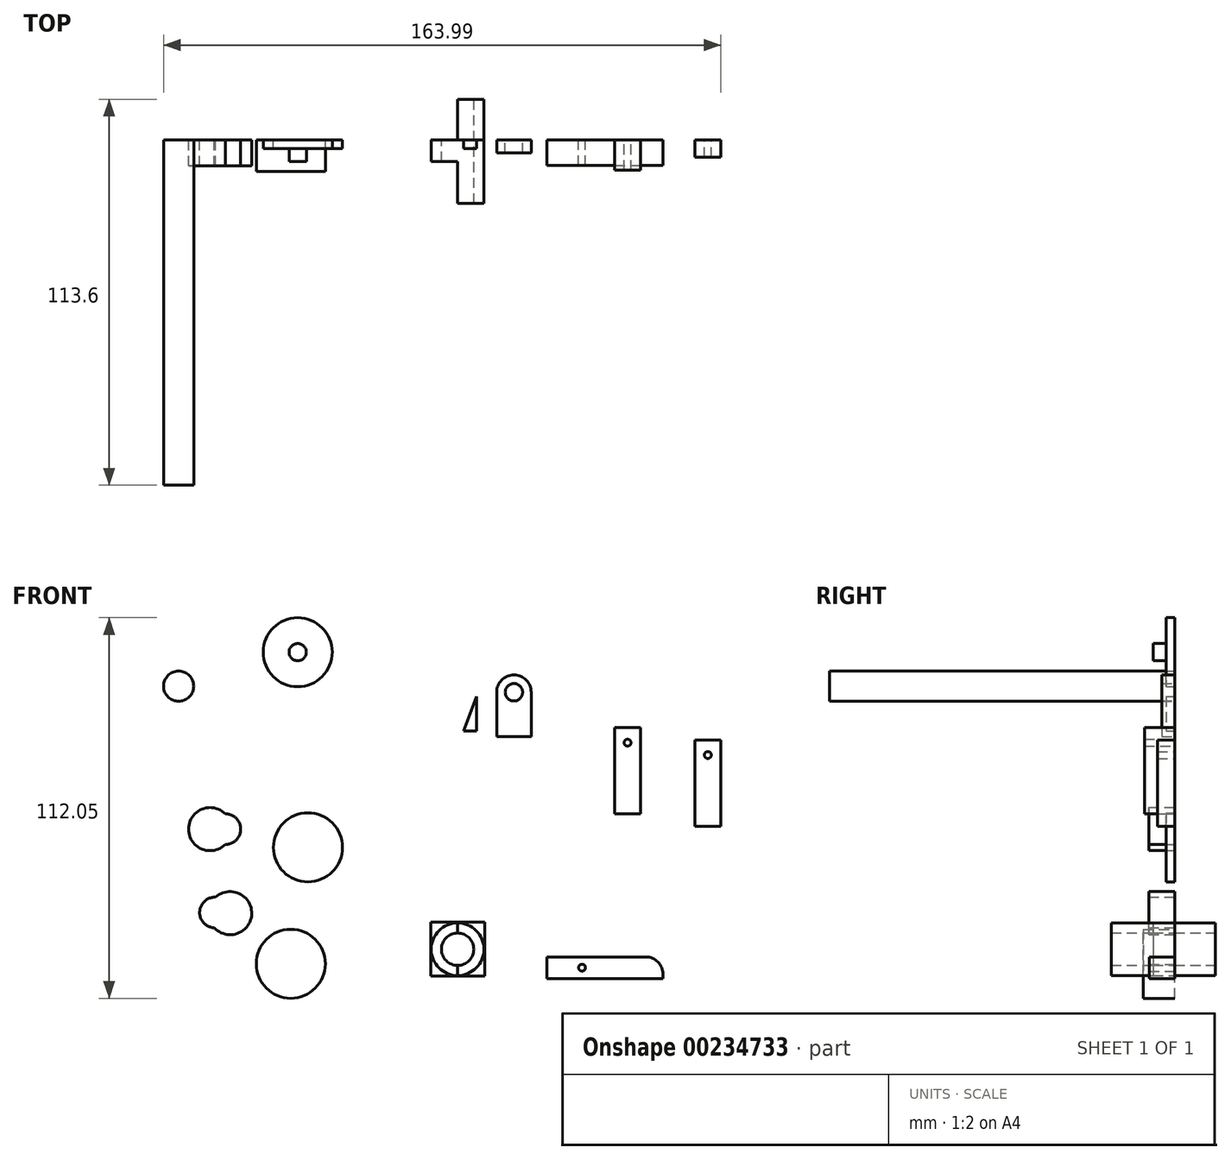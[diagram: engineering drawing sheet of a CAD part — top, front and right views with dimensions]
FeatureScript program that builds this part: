
annotation { "Feature Type Name" : "Feature", "Feature Type Description" : "" }
export const myFeature = defineFeature(function(context is Context, id is Id, definition is map)
    precondition{}
    {
        {
            var Q0;
            Q0=qCreatedBy(makeId("Front.planeOp"),FACE);
            var sketch = newSketch(context, id + "F0", { "sketchPlane" : qUnion([Q0])});
            skLineSegment(sketch, "E0.bottom", {"start": v(-88.6, 67.1) * mm, "end": v(-25.1, 67.1) * mm});
            skLineSegment(sketch, "E0.top", {"start": v(-88.6, 60.75) * mm, "end": v(-25.1, 60.75) * mm});
            skLineSegment(sketch, "E0.left", {"start": v(-88.6, 67.1) * mm, "end": v(-88.6, 60.75) * mm});
            skLineSegment(sketch, "E0.right", {"start": v(-25.1, 67.1) * mm, "end": v(-25.1, 60.75) * mm});
            skLineSegment(sketch, "E1.bottom", {"start": v(5.5, -31.9) * mm, "end": v(21.38, -31.9) * mm});
            skLineSegment(sketch, "E1.top", {"start": v(5.5, -47.78) * mm, "end": v(21.38, -47.78) * mm});
            skLineSegment(sketch, "E1.left", {"start": v(5.5, -31.9) * mm, "end": v(5.5, -47.78) * mm});
            skLineSegment(sketch, "E1.right", {"start": v(21.38, -31.9) * mm, "end": v(21.38, -47.78) * mm});
            skLineSegment(sketch, "E2.bottom", {"start": v(39.75, -42.1) * mm, "end": v(73.87, -42.1) * mm});
            skLineSegment(sketch, "E2.top", {"start": v(39.75, -48.45) * mm, "end": v(73.87, -48.45) * mm});
            skLineSegment(sketch, "E2.left", {"start": v(39.75, -42.1) * mm, "end": v(39.75, -48.45) * mm});
            skLineSegment(sketch, "E2.right", {"start": v(73.87, -42.1) * mm, "end": v(73.87, -48.45) * mm});
            skCircle(sketch, "E3", {"center": v(13.44, -39.84) * mm, "radius": 4.76 * mm});
            skPoint(sketch, "E3.centerSnap0", {"position": v(13.44, -31.9) * mm});
            skPoint(sketch, "E3.centerSnap1", {"position": v(5.5, -39.84) * mm});
            skCircle(sketch, "E4", {"center": v(-53.5, -29.22) * mm, "radius": 6.35 * mm});
            skArc(sketch, "E5", {"start": v(-57.8, -24.54) * mm, "mid": v(-62.48, -28.85) * mm, "end": v(-58.17, -33.52) * mm});
            skCircle(sketch, "E6", {"center": v(-35.65, -44.13) * mm, "radius": 10.16 * mm});
            skCircle(sketch, "E7", {"center": v(50.06, -45.27) * mm, "radius": 1.02 * mm});
            skCircle(sketch, "E8", {"center": v(-30.62, -9.86) * mm, "radius": 10.16 * mm});
            skCircle(sketch, "E9", {"center": v(-33.63, 47.6) * mm, "radius": 10.16 * mm});
            skCircle(sketch, "E10", {"center": v(-33.63, 47.6) * mm, "radius": 2.54 * mm});
            skLineSegment(sketch, "E11.bottom", {"start": v(24.93, 40.87) * mm, "end": v(35.1, 40.87) * mm});
            skLineSegment(sketch, "E11.top", {"start": v(24.93, 22.76) * mm, "end": v(35.1, 22.76) * mm});
            skLineSegment(sketch, "E11.left", {"start": v(24.93, 40.87) * mm, "end": v(24.93, 22.76) * mm});
            skLineSegment(sketch, "E11.right", {"start": v(35.1, 40.87) * mm, "end": v(35.1, 22.76) * mm});
            skCircle(sketch, "E12", {"center": v(30.01, 35.8) * mm, "radius": 2.56 * mm});
            skLineSegment(sketch, "E13", {"start": v(30.01, 35.8) * mm, "end": v(35.1, 35.8) * mm});
            skLineSegment(sketch, "E14", {"start": v(30.01, 35.8) * mm, "end": v(24.93, 35.8) * mm});
            skLineSegment(sketch, "E15", {"start": v(19.02, 34.56) * mm, "end": v(19.02, 24.4) * mm});
            skLineSegment(sketch, "E16", {"start": v(19.02, 24.4) * mm, "end": v(15.21, 24.4) * mm});
            skLineSegment(sketch, "E17", {"start": v(15.21, 24.4) * mm, "end": v(19.02, 34.56) * mm});
            skCircle(sketch, "E18", {"center": v(-59.4, -4.5) * mm, "radius": 6.35 * mm});
            skArc(sketch, "E19", {"start": v(-54.9, -8.98) * mm, "mid": v(-50.41, -4.5) * mm, "end": v(-54.9, 0) * mm});
            skLineSegment(sketch, "E20.bottom", {"start": v(83.25, 21.77) * mm, "end": v(90.87, 21.77) * mm});
            skLineSegment(sketch, "E20.top", {"start": v(83.25, -3.63) * mm, "end": v(90.87, -3.63) * mm});
            skLineSegment(sketch, "E20.left", {"start": v(83.25, 21.77) * mm, "end": v(83.25, -3.63) * mm});
            skLineSegment(sketch, "E20.right", {"start": v(90.87, 21.77) * mm, "end": v(90.87, -3.63) * mm});
            skCircle(sketch, "E21", {"center": v(87.06, 17.33) * mm, "radius": 1.02 * mm});
            skLineSegment(sketch, "E22", {"start": v(86.05, 17.33) * mm, "end": v(83.25, 17.33) * mm});
            skLineSegment(sketch, "E23", {"start": v(88.08, 17.33) * mm, "end": v(90.87, 17.33) * mm});
            skPoint(sketch, "E23.endSnap0", {"position": v(90.87, 9.07) * mm});
            skLineSegment(sketch, "E24.bottom", {"start": v(59.65, 25.4) * mm, "end": v(67.27, 25.4) * mm});
            skLineSegment(sketch, "E24.top", {"start": v(59.65, 0) * mm, "end": v(67.27, 0) * mm});
            skLineSegment(sketch, "E24.left", {"start": v(59.65, 25.4) * mm, "end": v(59.65, 0) * mm});
            skLineSegment(sketch, "E24.right", {"start": v(67.27, 25.4) * mm, "end": v(67.27, 0) * mm});
            skCircle(sketch, "E25", {"center": v(63.44, 20.96) * mm, "radius": 1.02 * mm});
            skLineSegment(sketch, "E26", {"start": v(62.47, 21.24) * mm, "end": v(59.65, 21.24) * mm});
            skLineSegment(sketch, "E27", {"start": v(64.46, 21) * mm, "end": v(67.27, 21) * mm});
            skCircle(sketch, "E28", {"center": v(-68.68, 37.58) * mm, "radius": 4.45 * mm});
            skCircle(sketch, "E29", {"center": v(13.44, -39.84) * mm, "radius": 7.75 * mm});
            skLineSegment(sketch, "E30", {"start": v(13.44, -35.08) * mm, "end": v(13.44, -32.1) * mm});
            skLineSegment(sketch, "E31", {"start": v(13.44, -44.6) * mm, "end": v(13.44, -47.6) * mm});
            skSolve(sketch);
        }
        {
            var Q0;
            Q0=makeQuery(id+"F0.imprint","IMPRINT",FACE,{"disambiguationData":[TD([[makeQuery(id+"F0.imprint","IMPRINT",EDGE,{"derivedFrom":sQuery(id+"F0.wireOp",EDGE,"E1.bottom")}),-1.0]])]});
            extrude(context, id + "F1", {"entities" : qUnion([Q0]), "depth" : 1 / 101.6 * mm});
        }
        {
            var Q0;
            Q0=makeQuery(id+"F0.imprint","IMPRINT",FACE,{"disambiguationData":[TD([[makeQuery(id+"F0.imprint","IMPRINT",EDGE,{"derivedFrom":sQuery(id+"F0.wireOp",EDGE,"E2.bottom")}),-1.0]])]});
            extrude(context, id + "F2", {"entities" : qUnion([Q0]), "depth" : 7.52 * mm});
        }
        {
            var Q0;
            {var subQ0=sQuery(id+"F0.wireOp",EDGE,"E5");var subQ1=sQuery(id+"F0.wireOp",EDGE,"E4");var subQ2=makeQuery(id+"F0.imprint","INTERSECT",VERTEX,{"disambiguationData":[OD(0.0)],"derivedFrom":[subQ1,subQ0]});Q0=makeQuery(id+"F0.imprint","IMPRINT",FACE,{"disambiguationData":[TD([[makeQuery(id+"F0.imprint","IMPRINT",EDGE,{"disambiguationData":[TD([[subQ2,-1.0]])],"derivedFrom":subQ1}),1.0]])]});}
            var Q1;
            {var subQ0=sQuery(id+"F0.wireOp",EDGE,"E5");Q1=makeQuery(id+"F0.imprint","IMPRINT",FACE,{"disambiguationData":[TD([[makeQuery(id+"F0.imprint","IMPRINT",EDGE,{"derivedFrom":subQ0}),1.0]])]});}
            extrude(context, id + "F3", {"entities" : qUnion([Q0, Q1]), "depth" : 7.62 * mm});
        }
        {
            var Q0;
            Q0=makeQuery(id+"F0.imprint","IMPRINT",FACE,{"disambiguationData":[TD([[makeQuery(id+"F0.imprint","IMPRINT",EDGE,{"derivedFrom":sQuery(id+"F0.wireOp",EDGE,"E6")}),1.0]])]});
            extrude(context, id + "F4", {"entities" : qUnion([Q0]), "depth" : 9.27 * mm});
        }
        {
            var Q0;
            Q0=makeQuery(id+"F2.opExtrude","SWEPT_EDGE",EDGE,{"disambiguationData":[OSD([sQuery(id+"F0.wireOp",EDGE,"E2.bottom"),sQuery(id+"F0.wireOp",EDGE,"E2.right")])]});
            fillet(context, id + "F5", {"entities" : qUnion([Q0]), "radius" : 5.08 * mm, "tangentPropagation" : true, "allowEdgeOverflow" : false});
        }
        {
            var Q0;
            Q0=makeQuery(id+"F0.imprint","IMPRINT",FACE,{"disambiguationData":[TD([[makeQuery(id+"F0.imprint","IMPRINT",EDGE,{"derivedFrom":sQuery(id+"F0.wireOp",EDGE,"E8")}),1.0]])]});
            extrude(context, id + "F6", {"entities" : qUnion([Q0]), "depth" : 2.54 * mm});
        }
        {
            var Q0;
            Q0=makeQuery(id+"F0.imprint","IMPRINT",FACE,{"disambiguationData":[TD([[makeQuery(id+"F0.imprint","IMPRINT",EDGE,{"derivedFrom":sQuery(id+"F0.wireOp",EDGE,"E10")}),1.0]])]});
            extrude(context, id + "F7", {"entities" : qUnion([Q0]), "depth" : 6.35 * mm});
        }
        {
            var Q0;
            Q0=makeQuery(id+"F0.imprint","IMPRINT",FACE,{"disambiguationData":[TD([[makeQuery(id+"F0.imprint","IMPRINT",EDGE,{"derivedFrom":sQuery(id+"F0.wireOp",EDGE,"E9")}),1.0]])]});
            extrude(context, id + "F8", {"entities" : qUnion([Q0]), "operationType" : NewBodyOperationType.ADD, "depth" : 2.54 * mm});
        }
        {
            var Q0;
            {var subQ6=sQuery(id+"F0.wireOp",EDGE,"E11.top");Q0=makeQuery(id+"F0.imprint","IMPRINT",FACE,{"disambiguationData":[TD([[makeQuery(id+"F0.imprint","IMPRINT",EDGE,{"derivedFrom":subQ6}),1.0]])]});}
            var Q1;
            {var subQ6=sQuery(id+"F0.wireOp",EDGE,"E11.bottom");Q1=makeQuery(id+"F0.imprint","IMPRINT",FACE,{"disambiguationData":[TD([[makeQuery(id+"F0.imprint","IMPRINT",EDGE,{"derivedFrom":subQ6}),-1.0]])]});}
            extrude(context, id + "F9", {"entities" : qUnion([Q0, Q1]), "depth" : 3.8 * mm});
        }
        {
            var Q0;
            Q0=makeQuery(id+"F0.imprint","IMPRINT",FACE,{"disambiguationData":[TD([[makeQuery(id+"F0.imprint","IMPRINT",EDGE,{"derivedFrom":sQuery(id+"F0.wireOp",EDGE,"E15")}),-1.0]])]});
            extrude(context, id + "F10", {"entities" : qUnion([Q0]), "depth" : 2.54 * mm});
        }
        {
            var Q0;
            Q0=makeQuery(id+"F9.opExtrude","SWEPT_EDGE",EDGE,{"disambiguationData":[OSD([sQuery(id+"F0.wireOp",EDGE,"E11.bottom"),sQuery(id+"F0.wireOp",EDGE,"E11.right")])]});
            var Q1;
            Q1=makeQuery(id+"F9.opExtrude","SWEPT_EDGE",EDGE,{"disambiguationData":[OSD([sQuery(id+"F0.wireOp",EDGE,"E11.bottom"),sQuery(id+"F0.wireOp",EDGE,"E11.left")])]});
            fillet(context, id + "F11", {"entities" : qUnion([Q0, Q1]), "radius" : 5.08 * mm, "tangentPropagation" : true, "allowEdgeOverflow" : false});
        }
        {
            var Q0;
            {var subQ0=sQuery(id+"F0.wireOp",EDGE,"E19");var subQ1=sQuery(id+"F0.wireOp",EDGE,"E18");var subQ2=makeQuery(id+"F0.imprint","INTERSECT",VERTEX,{"disambiguationData":[OD(0.0)],"derivedFrom":[subQ1,subQ0]});Q0=makeQuery(id+"F0.imprint","IMPRINT",FACE,{"disambiguationData":[TD([[makeQuery(id+"F0.imprint","IMPRINT",EDGE,{"disambiguationData":[TD([[subQ2,1.0]])],"derivedFrom":subQ1}),1.0]])]});}
            var Q1;
            {var subQ0=sQuery(id+"F0.wireOp",EDGE,"E19");Q1=makeQuery(id+"F0.imprint","IMPRINT",FACE,{"disambiguationData":[TD([[makeQuery(id+"F0.imprint","IMPRINT",EDGE,{"derivedFrom":subQ0}),1.0]])]});}
            extrude(context, id + "F12", {"entities" : qUnion([Q0, Q1]), "depth" : 7.62 * mm});
        }
        {
            var Q0;
            {var subQ4=sQuery(id+"F0.wireOp",EDGE,"E20.bottom");Q0=makeQuery(id+"F0.imprint","IMPRINT",FACE,{"disambiguationData":[TD([[makeQuery(id+"F0.imprint","IMPRINT",EDGE,{"derivedFrom":subQ4}),-1.0]])]});}
            var Q1;
            {var subQ4=sQuery(id+"F0.wireOp",EDGE,"E20.top");Q1=makeQuery(id+"F0.imprint","IMPRINT",FACE,{"disambiguationData":[TD([[makeQuery(id+"F0.imprint","IMPRINT",EDGE,{"derivedFrom":subQ4}),1.0]])]});}
            extrude(context, id + "F13", {"entities" : qUnion([Q0, Q1]), "depth" : 5.08 * mm});
        }
        {
            var Q0;
            {var subQ4=sQuery(id+"F0.wireOp",EDGE,"E24.bottom");Q0=makeQuery(id+"F0.imprint","IMPRINT",FACE,{"disambiguationData":[TD([[makeQuery(id+"F0.imprint","IMPRINT",EDGE,{"derivedFrom":subQ4}),-1.0]])]});}
            var Q1;
            {var subQ4=sQuery(id+"F0.wireOp",EDGE,"E24.top");Q1=makeQuery(id+"F0.imprint","IMPRINT",FACE,{"disambiguationData":[TD([[makeQuery(id+"F0.imprint","IMPRINT",EDGE,{"derivedFrom":subQ4}),1.0]])]});}
            extrude(context, id + "F14", {"entities" : qUnion([Q0, Q1]), "depth" : 8.9 * mm});
        }
        {
            var Q0;
            Q0=makeQuery(id+"F0.imprint","IMPRINT",FACE,{"disambiguationData":[TD([[makeQuery(id+"F0.imprint","IMPRINT",EDGE,{"derivedFrom":sQuery(id+"F0.wireOp",EDGE,"E28")}),1.0]])]});
            extrude(context, id + "F15", {"entities" : qUnion([Q0]), "depth" : 101.6 * mm});
        }
        {
            var Q0;
            {var subQ0=sQuery(id+"F0.wireOp",EDGE,"E30");Q0=makeQuery(id+"F0.imprint","IMPRINT",FACE,{"disambiguationData":[TD([[makeQuery(id+"F0.imprint","IMPRINT",EDGE,{"derivedFrom":subQ0}),1.0]])]});}
            extrude(context, id + "F16", {"entities" : qUnion([Q0]), "operationType" : NewBodyOperationType.ADD, "depth" : 6.35 * mm});
        }
        {
            var Q0;
            {var subQ0=sQuery(id+"F0.wireOp",EDGE,"E30");Q0=makeQuery(id+"F0.imprint","IMPRINT",FACE,{"disambiguationData":[TD([[makeQuery(id+"F0.imprint","IMPRINT",EDGE,{"derivedFrom":subQ0}),-1.0]])]});}
            extrude(context, id + "F17", {"entities" : qUnion([Q0]), "operationType" : NewBodyOperationType.ADD, "depth" : 18.7 * mm, "hasSecondDirection" : true, "secondDirectionOppositeDirection" : true, "secondDirectionDepth" : 12 * mm});
        }
    });
